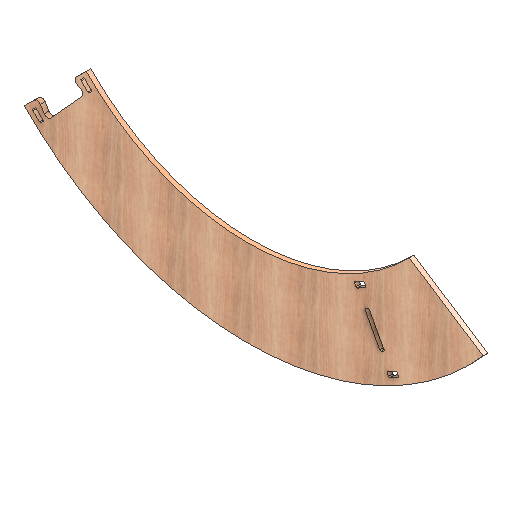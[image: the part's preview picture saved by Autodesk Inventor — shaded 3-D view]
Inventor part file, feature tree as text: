
AUTODESK INVENTOR PART (.ipt)
format: ipt  version: 2021 (Build 250183000, 183)  size: 323,584 bytes
history: native  units: mm
features: other x2, extrude x2, hole x1
ambient origin geometry x8: Origin, YZ Plane, XZ Plane, XY Plane, X Axis, Y Axis, Z Axis, Center Point
bodies: Body1 (feature_tree)
feature tree (5):
  other  "CONTOURS"
  hole  "HOLES"  [1 undecoded]
  other  "LETTERS"
  extrude  "Extrusion3"  Depth=18.0mm TaperAngle=0.0deg
  extrude  "Extrusion4"  [1 undecoded]
note: 2 required parameter values undecoded (feature->parameter linkage not recoverable at this tier; creation-order binding heuristic only, values carry confidence <= 0.55)
